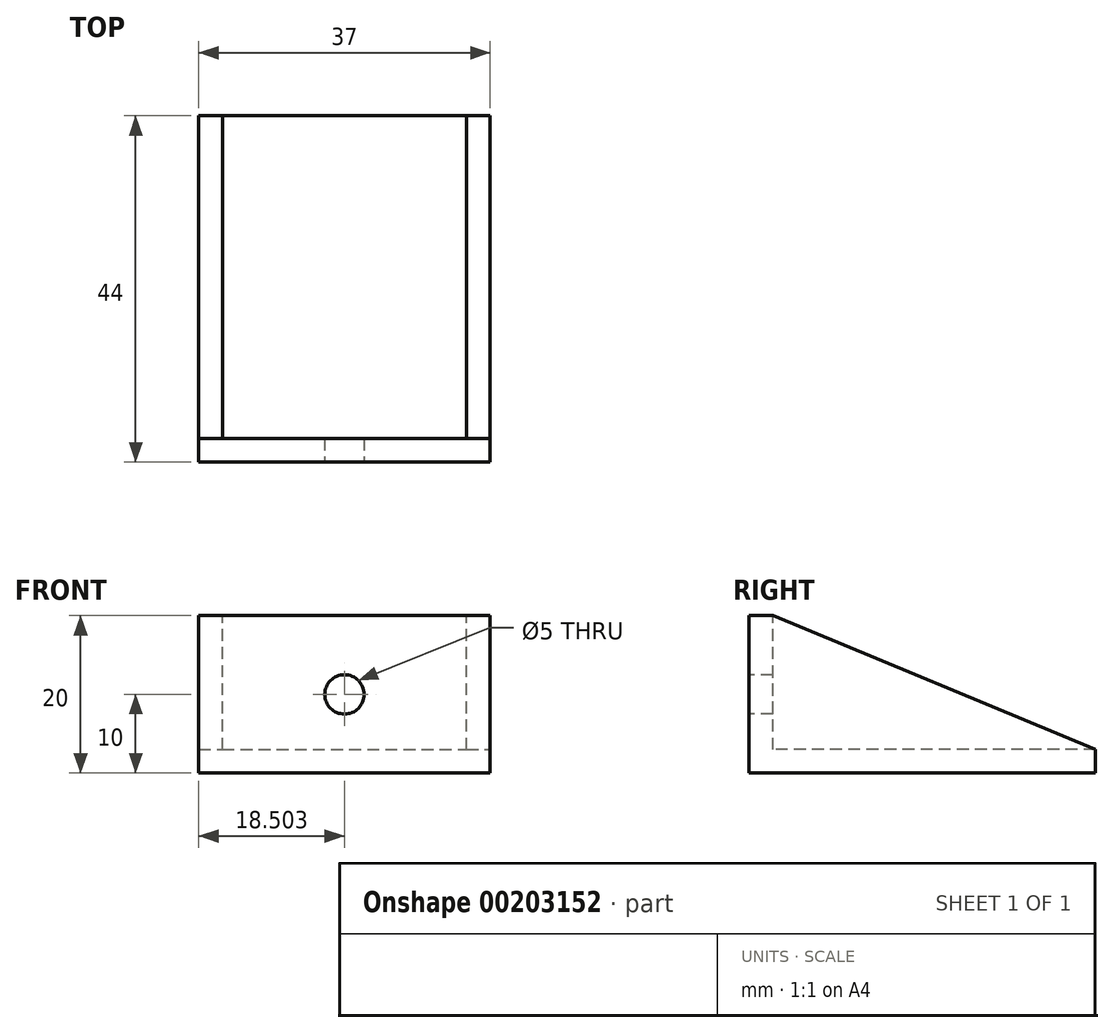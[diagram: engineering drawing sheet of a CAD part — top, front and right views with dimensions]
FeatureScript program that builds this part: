
annotation { "Feature Type Name" : "Feature", "Feature Type Description" : "" }
export const myFeature = defineFeature(function(context is Context, id is Id, definition is map)
    precondition{}
    {
        {
            var Q0;
            Q0=qCreatedBy(makeId("Top.planeOp"),FACE);
            var sketch = newSketch(context, id + "F0", { "sketchPlane" : qUnion([Q0])});
            skLineSegment(sketch, "E0.bottom", {"start": v(-22.5, 22.25) * mm, "end": v(14.5, 22.25) * mm});
            skLineSegment(sketch, "E0.top", {"start": v(-22.5, -21.75) * mm, "end": v(14.5, -21.75) * mm});
            skLineSegment(sketch, "E0.left", {"start": v(-22.5, 22.25) * mm, "end": v(-22.5, -21.75) * mm});
            skLineSegment(sketch, "E0.right", {"start": v(14.5, 22.25) * mm, "end": v(14.5, -21.75) * mm});
            skSolve(sketch);
        }
        {
            var Q0;
            Q0=makeQuery(id+"F0.imprint","IMPRINT",FACE,{"disambiguationData":[TD([[makeQuery(id+"F0.imprint","IMPRINT",EDGE,{"derivedFrom":sQuery(id+"F0.wireOp",EDGE,"E0.bottom")}),-1.0]])]});
            extrude(context, id + "F1", {"entities" : qUnion([Q0]), "depth" : 3 * mm});
        }
        {
            var Q0;
            Q0=makeQuery(id+"F1.opExtrude","SWEPT_FACE",FACE,{"disambiguationData":[OSD([sQuery(id+"F0.wireOp",EDGE,"E0.top")])]});
            var sketch = newSketch(context, id + "F2", { "sketchPlane" : qUnion([Q0])});
            skLineSegment(sketch, "E1.bottom", {"start": v(-22.5, 3) * mm, "end": v(14.5, 3) * mm});
            skLineSegment(sketch, "E1.top", {"start": v(-22.5, 20) * mm, "end": v(14.5, 20) * mm});
            skLineSegment(sketch, "E1.left", {"start": v(-22.5, 3) * mm, "end": v(-22.5, 20) * mm});
            skLineSegment(sketch, "E1.right", {"start": v(14.5, 3) * mm, "end": v(14.5, 20) * mm});
            skSolve(sketch);
        }
        {
            var Q0;
            Q0=makeQuery(id+"F2.imprint","IMPRINT",FACE,{"disambiguationData":[TD([[makeQuery(id+"F2.imprint","IMPRINT",EDGE,{"derivedFrom":sQuery(id+"F2.wireOp",EDGE,"E1.bottom")}),1.0]])]});
            extrude(context, id + "F3", {"entities" : qUnion([Q0]), "operationType" : NewBodyOperationType.ADD, "oppositeDirection" : true, "depth" : 3 * mm});
        }
        {
            var Q0;
            Q0=makeQuery(id+"F3.boolean.opBoolean","MERGE",FACE,{"derivedFrom":[makeQuery(id+"F1.opExtrude","SWEPT_FACE",FACE,{"disambiguationData":[OSD([sQuery(id+"F0.wireOp",EDGE,"E0.right")])]}),makeQuery(id+"F3.opExtrude","SWEPT_FACE",FACE,{"disambiguationData":[OSD([sQuery(id+"F2.wireOp",EDGE,"E1.right")])]})]});
            var sketch = newSketch(context, id + "F4", { "sketchPlane" : qUnion([Q0])});
            skLineSegment(sketch, "E2", {"start": v(-18.75, 20) * mm, "end": v(22.25, 3) * mm});
            skSolve(sketch);
        }
        {
            var Q0;
            Q0=makeQuery(id+"F4.imprint","IMPRINT",FACE,{"disambiguationData":[TD([[makeQuery(id+"F4.imprint","IMPRINT",EDGE,{"derivedFrom":sQuery(id+"F4.wireOp",EDGE,"E2")}),-1.0]])]});
            extrude(context, id + "F5", {"entities" : qUnion([Q0]), "operationType" : NewBodyOperationType.ADD, "oppositeDirection" : true, "depth" : 3 * mm});
        }
        {
            var Q0;
            Q0=makeQuery(id+"F3.boolean.opBoolean","MERGE",FACE,{"derivedFrom":[makeQuery(id+"F1.opExtrude","SWEPT_FACE",FACE,{"disambiguationData":[OSD([sQuery(id+"F0.wireOp",EDGE,"E0.left")])]}),makeQuery(id+"F3.opExtrude","SWEPT_FACE",FACE,{"disambiguationData":[OSD([sQuery(id+"F2.wireOp",EDGE,"E1.left")])]})]});
            var sketch = newSketch(context, id + "F6", { "sketchPlane" : qUnion([Q0])});
            skLineSegment(sketch, "E3", {"start": v(18.75, 20) * mm, "end": v(-22.25, 3) * mm});
            skSolve(sketch);
        }
        {
            var Q0;
            Q0=makeQuery(id+"F6.imprint","IMPRINT",FACE,{"disambiguationData":[TD([[makeQuery(id+"F6.imprint","IMPRINT",EDGE,{"derivedFrom":sQuery(id+"F6.wireOp",EDGE,"E3")}),1.0]])]});
            extrude(context, id + "F7", {"entities" : qUnion([Q0]), "operationType" : NewBodyOperationType.ADD, "oppositeDirection" : true, "depth" : 3 * mm});
        }
        {
            var Q0;
            Q0=makeQuery(id+"F3.boolean.opBoolean","MERGE",FACE,{"derivedFrom":[makeQuery(id+"F1.opExtrude","SWEPT_FACE",FACE,{"disambiguationData":[OSD([sQuery(id+"F0.wireOp",EDGE,"E0.top")])]}),makeQuery(id+"F3.opExtrude","CAP_FACE",FACE,{"disambiguationData":[OSD([sQuery(id+"F2.wireOp",EDGE,"E1.bottom"),sQuery(id+"F2.wireOp",EDGE,"E1.top"),sQuery(id+"F2.wireOp",EDGE,"E1.left"),sQuery(id+"F2.wireOp",EDGE,"E1.right")])],"isStart":true})]});
            var sketch = newSketch(context, id + "F8", { "sketchPlane" : qUnion([Q0])});
            skLineSegment(sketch, "E4", {"start": v(14.5, 20) * mm, "end": v(-22.5, 0) * mm});
            skLineSegment(sketch, "E5", {"start": v(-22.5, 0) * mm, "end": v(-22.5, 20) * mm});
            skLineSegment(sketch, "E6", {"start": v(-22.5, 20) * mm, "end": v(14.5, 0) * mm});
            skCircle(sketch, "E7", {"center": v(-4, 10) * mm, "radius": 2.62 * mm});
            skSolve(sketch);
        }
        {
            var Q0;
            Q0=sQuery(id+"F8.wireOp",VERTEX,"E7.center");
            var Q1;
            Q1=makeQuery(id+"F1.opExtrude","SWEPT_BODY",BODY,{"disambiguationData":[OSD([sQuery(id+"F0.wireOp",EDGE,"E0.bottom"),sQuery(id+"F0.wireOp",EDGE,"E0.top"),sQuery(id+"F0.wireOp",EDGE,"E0.left"),sQuery(id+"F0.wireOp",EDGE,"E0.right")])]});
            hole(context, id + "F9", {"style" : HoleStyle.SIMPLE, "endStyle" : HoleEndStyle.THROUGH, "holeDiameter" : 5 * mm, "locations" : qUnion([Q0]), "scope" : qUnion([Q1]), "isTappedThrough" : true});
        }
    });
